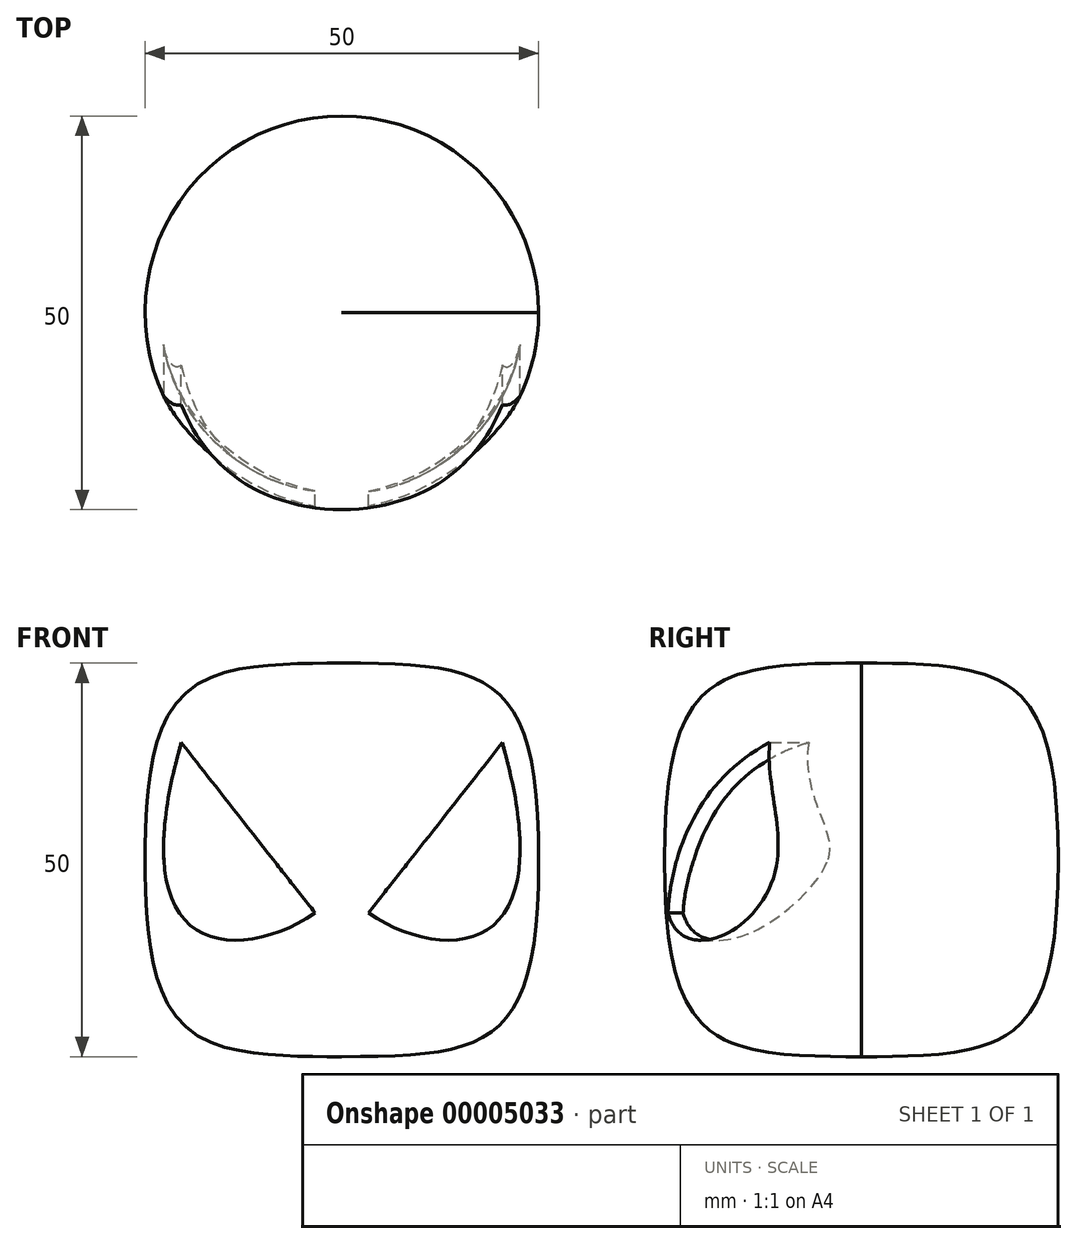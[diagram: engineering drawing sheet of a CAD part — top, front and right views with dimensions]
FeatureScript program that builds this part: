
annotation { "Feature Type Name" : "Feature", "Feature Type Description" : "" }
export const myFeature = defineFeature(function(context is Context, id is Id, definition is map)
    precondition{}
    {
        {
            var Q0;
            Q0=qCreatedBy(makeId("Front.planeOp"),FACE);
            var sketch = newSketch(context, id + "F0", { "sketchPlane" : qUnion([Q0])});
            skLineSegment(sketch, "E0", {"start": v(0, 0) * mm, "end": v(0, 25) * mm, "construction": true});
            skLineSegment(sketch, "E1", {"start": v(0, 0) * mm, "end": v(25, 0) * mm, "construction": true});
            skFitSpline(sketch, "E2", {"points": [v(0, 25) * mm, v(25, 0) * mm], "startDerivative": vector(56.82, 0) * mm, "endDerivative": vector(0, -71.1) * mm});
            skFitSpline(sketch, "E3.0.MirrorCS", {"points": [v(0, -25) * mm, v(25, 0) * mm], "startDerivative": vector(56.82, 0) * mm, "endDerivative": vector(0, 71.1) * mm});
            skLineSegment(sketch, "E4", {"start": v(0, 25) * mm, "end": v(0, -25) * mm});
            skFitSpline(sketch, "E5.0", {"points": [v(0, -23) * mm, v(2.36, -23) * mm, v(6.64, -22.96) * mm, v(10.94, -22.6) * mm, v(13.76, -22.06) * mm, v(15.56, -21.5) * mm, v(17.08, -20.78) * mm, v(18.34, -19.9) * mm, v(19.42, -18.8) * mm, v(20.36, -17.41) * mm, v(21.17, -15.66) * mm, v(22.07, -12.77) * mm, v(22.81, -8.04) * mm, v(23, -2.92) * mm, v(23, 0) * mm]});
            skFitSpline(sketch, "E5.1", {"points": [v(0, 23) * mm, v(2.36, 23) * mm, v(6.64, 22.96) * mm, v(10.94, 22.6) * mm, v(13.76, 22.06) * mm, v(15.56, 21.5) * mm, v(17.08, 20.78) * mm, v(18.34, 19.9) * mm, v(19.42, 18.8) * mm, v(20.36, 17.41) * mm, v(21.17, 15.66) * mm, v(22.07, 12.77) * mm, v(22.81, 8.04) * mm, v(23, 2.92) * mm, v(23, 0) * mm]});
            skSolve(sketch);
        }
        {
            var Q0;
            {var subQ1=sQuery(id+"F0.wireOp",EDGE,"E5.0");Q0=makeQuery(id+"F0.imprint","IMPRINT",FACE,{"disambiguationData":[TD([[makeQuery(id+"F0.imprint","IMPRINT",EDGE,{"derivedFrom":subQ1}),1.0]])]});}
            var Q1;
            {var subQ4=sQuery(id+"F0.wireOp",EDGE,"E2");Q1=makeQuery(id+"F0.imprint","IMPRINT",FACE,{"disambiguationData":[TD([[makeQuery(id+"F0.imprint","IMPRINT",EDGE,{"derivedFrom":subQ4}),-1.0]])]});}
            var Q2;
            Q2=sQuery(id+"F0.wireOp",EDGE,"E4");
            revolve(context, id + "F1", {"entities" : qUnion([Q0, Q1]), "axis" : qUnion([Q2]), "revolveType" : RevolveType.FULL});
        }
        {
            var Q0;
            Q0=qCreatedBy(makeId("Front.planeOp"),FACE);
            var sketch = newSketch(context, id + "F2", { "sketchPlane" : qUnion([Q0])});
            skFitSpline(sketch, "E6", {"points": [v(20.4, 14.89) * mm, v(3.4, -6.73) * mm], "startDerivative": vector(25.57, -89.69) * mm, "endDerivative": vector(-22.96, 16.45) * mm});
            skLineSegment(sketch, "E7", {"start": v(20.4, 14.89) * mm, "end": v(3.4, -6.73) * mm});
            skLineSegment(sketch, "E8.0.MirrorCS", {"start": v(-20.4, 14.89) * mm, "end": v(-3.4, -6.73) * mm});
            skFitSpline(sketch, "E9.0.MirrorCS", {"points": [v(-20.4, 14.89) * mm, v(-3.4, -6.73) * mm], "startDerivative": vector(-25.57, -89.69) * mm, "endDerivative": vector(22.96, 16.45) * mm});
            skSolve(sketch);
        }
        {
            var Q0;
            Q0=qSketchRegion(id+"F2",true);
            extrude(context, id + "F3", {"entities" : qUnion([Q0]), "operationType" : NewBodyOperationType.REMOVE, "depth" : 25 * mm});
        }
        {
            var Q0;
            {var subQ1=sQuery(id+"F0.wireOp",EDGE,"E5.0");Q0=makeQuery(id+"F0.imprint","IMPRINT",FACE,{"disambiguationData":[TD([[makeQuery(id+"F0.imprint","IMPRINT",EDGE,{"derivedFrom":subQ1}),1.0]])]});}
            var Q1;
            Q1=sQuery(id+"F0.wireOp",EDGE,"E4");
            revolve(context, id + "F4", {"operationType" : NewBodyOperationType.ADD, "entities" : qUnion([Q0]), "axis" : qUnion([Q1]), "revolveType" : RevolveType.FULL});
        }
    });
